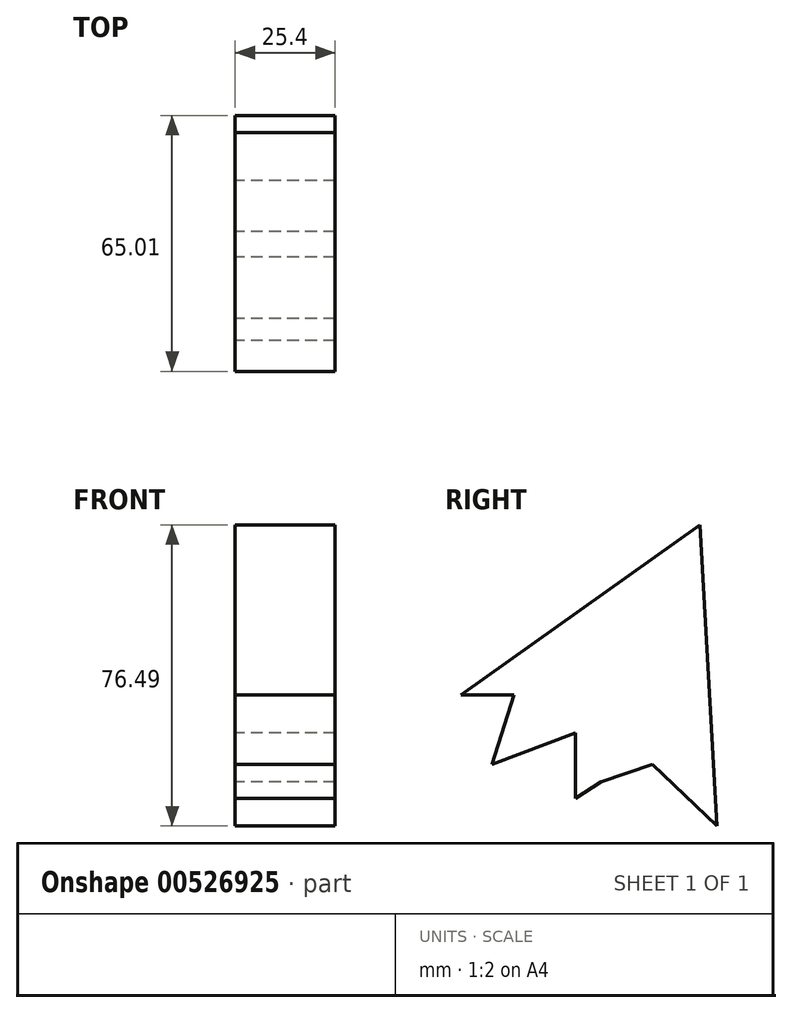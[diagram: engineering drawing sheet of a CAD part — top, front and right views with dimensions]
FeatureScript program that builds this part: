
annotation { "Feature Type Name" : "Feature", "Feature Type Description" : "" }
export const myFeature = defineFeature(function(context is Context, id is Id, definition is map)
    precondition{}
    {
        {
            var Q0;
            Q0=qCreatedBy(makeId("Right.planeOp"),FACE);
            var sketch = newSketch(context, id + "F0", { "sketchPlane" : qUnion([Q0])});
            skLineSegment(sketch, "E0", {"start": v(12.14, 60.9) * mm, "end": v(-48.55, 17.66) * mm});
            skLineSegment(sketch, "E1", {"start": v(12.14, 60.9) * mm, "end": v(16.46, -15.59) * mm});
            skLineSegment(sketch, "E2", {"start": v(-48.55, 17.66) * mm, "end": v(-35.08, 17.66) * mm});
            skLineSegment(sketch, "E3", {"start": v(-35.08, 17.66) * mm, "end": v(-40.71, 0) * mm});
            skLineSegment(sketch, "E4", {"start": v(-40.71, 0) * mm, "end": v(-19.49, 8.04) * mm});
            skLineSegment(sketch, "E5", {"start": v(-19.49, 8.04) * mm, "end": v(-19.49, -8.61) * mm});
            skLineSegment(sketch, "E6", {"start": v(-13, -4.36) * mm, "end": v(-19.49, -8.61) * mm});
            skLineSegment(sketch, "E7", {"start": v(-13, -4.36) * mm, "end": v(0, 0) * mm});
            skLineSegment(sketch, "E8", {"start": v(0, 0) * mm, "end": v(16.46, -15.59) * mm});
            skSolve(sketch);
        }
        {
            var Q0;
            Q0 = qSketchRegion(id + "F0", true);
            extrude(context, id + "F1", {"entities" : qUnion([Q0]), "depth" : 25.4 * mm, "offsetDistance" : 25.4 * mm});
        }
    });
